# Revit family: Hager-VECTOR-Surface_mounted-IP65-With_Cover-With_DIN-NoHosted-ES-es
name_source: partatom
category: Electrical Equipment
units: mm (PartAtom-declared; Revit-internal decimal feet)

## family parameters
Always vertical = Yes
Cut with Voids When Loaded = No
Maintain Annotation Orientation = No
Panel Configuration = Two Columns, Circuits Across
Part Type = Panelboard
Room Calculation Point = No
Round Connector Dimension = Use Diameter
Shared = No
Work Plane-Based = Yes

## types (52) — shared parameters
Code hager = ADD-EC000214_EU
Default Elevation = 1200 mm
EF000003 - Método de montaje = Montado superficial (escayola)
EF000007 - Color = Gris
EF000024 - Resistente a UV = No
EF000116 - Número RAL = 7035
EF000118 - Con placa de montaje = No
EF001062 - Versión de CEM = No
EF001134 - Carril DIN = Yes
EF004462 - Tipo de cierre = Otros
EF005474 - Grado de protección (IP) = IP65
EF006306 - Con candado = No
ETIM class code = EC000214
ETIM class name = Small distribution board
HG000001 - Número de columnas = 1
HG000002-with door or cover-es = Yes
HG000003-Range-es = VECTOR
HG000005-Thickness-es = 2 mm  [stored 0.00656168 ft]
HG000006-Flush mounted-es = No
HG000009-Double swing door-es = No
HG000010-Asymmetric doors-es = No
HG000011-Empty rows from bottom-es = No
HG000012-Door swing angle-es = 90.00°
HG000013-Door on the left-es = No
HG000014-Door on the right-es = Yes
HG000015-Clearance visibility-es = Yes
HG000016-Door 3D visibility-es = Yes
HG000017-Distance between poles-es = 18 mm  [stored 0.0590551 ft]
HG000060-RAL-number = 7035
HG000099-Onfly Template ID-es-ES = 507532
Manufacturer = Hager
Name BIM&CO = Electricity
Name hager = ADD_Enclosures_EC000214
Reference = Template-Enclosure_EU-EC000214
Uniformat = Low Tension Service & Dist.
Uniformat code = D501001
zero-valued in all types: EF000218 - Profundidad de instalación, EF000332 - Altura de la instalación, EF000846 - Anchura de montaje, EF001131 - Profundidad interna, HG000007-Number of empty columns-es, HG000008-Number of empty rows-es

## per-type parameters (varying)
| type | BC_METADATA | EF000008 - Anchura | EF000040 - Altura | EF000049 - Profundidad | EF000266 - Número de filas | EF001088 - Posibilidad de extensión | EF002950 - Ancho en número de espacios modulares | EF006244 - Tapa/puerta transparente | EF009212 - Versión de la cubierta | EF015776 - Borne de tierra | EF015777 - Borne neutro | EF015941 - Puerta de transmisión de señal | HG000004-Manufacturer reference-es | HGEF000266-Número de filas | HGEF0002950-Ancho en número de espacios modulares |
| VECTOR-Surface_mounted_W310_H552_D151_12_Modular_Spacing-VE312F | {"ObjectGuid":"7676197e-38a1-4d90-8ddf-f4d718d94560","ModelGuid":"2ff45430-9ef3-4878-b9e2-60a5c988bfcc","VariantGuid":"09c07b7e-c6df-4300-81fb-90c715c4e884","Revision":"#6","VariantName":"VECTOR-Surface_mounted_W310_H552_D151_12_Modular_Spacing-VE312F"} | 310 mm  [stored 1.01706 ft] | 552 mm  [stored 1.81102 ft] | 151 mm  [stored 0.495407 ft] | 3 | Yes | 12 | No | Cerrado | Yes | No | Yes | VE312F | 3 | 12 |
| VECTOR-Surface_mounted_W310_H552_D151_12_Modular_Spacing-VE312PN | {"ObjectGuid":"7676197e-38a1-4d90-8ddf-f4d718d94560","ModelGuid":"2ff45430-9ef3-4878-b9e2-60a5c988bfcc","VariantGuid":"d662e2b3-0be1-45da-8c5f-6823ab68ee60","Revision":"#6","VariantName":"VECTOR-Surface_mounted_W310_H552_D151_12_Modular_Spacing-VE312PN"} | 310 mm  [stored 1.01706 ft] | 552 mm  [stored 1.81102 ft] | 151 mm  [stored 0.495407 ft] | 3 | Yes | 12 | Yes | Cerrado | No | No | Yes | VE312PN | 3 | 12 |
| VECTOR-Surface_mounted_W310_H552_D151_12_Modular_Spacing-VE312S | {"ObjectGuid":"7676197e-38a1-4d90-8ddf-f4d718d94560","ModelGuid":"2ff45430-9ef3-4878-b9e2-60a5c988bfcc","VariantGuid":"74c3a6b9-71b7-44c3-8c2b-f7d0cc669d50","Revision":"#6","VariantName":"VECTOR-Surface_mounted_W310_H552_D151_12_Modular_Spacing-VE312S"} | 310 mm  [stored 1.01706 ft] | 552 mm  [stored 1.81102 ft] | 151 mm  [stored 0.495407 ft] | 3 | Yes | 12 | No | Cerrado | Yes | Yes | Yes | VE312S | 3 | 12 |
| VECTOR-Surface_mounted_W310_H552_D151_12_Modular_Spacing-VE312SN | {"ObjectGuid":"7676197e-38a1-4d90-8ddf-f4d718d94560","ModelGuid":"2ff45430-9ef3-4878-b9e2-60a5c988bfcc","VariantGuid":"e56d686b-ab52-4e53-b856-6d5e133bc343","Revision":"#6","VariantName":"VECTOR-Surface_mounted_W310_H552_D151_12_Modular_Spacing-VE312SN"} | 310 mm  [stored 1.01706 ft] | 552 mm  [stored 1.81102 ft] | 151 mm  [stored 0.495407 ft] | 3 | Yes | 12 | Yes | Con muesca | No | No | Yes | VE312SN | 3 | 12 |
| VECTOR-Surface_mounted_W310_H552_D151_36_Modular_Spacing-VE312YN | {"ObjectGuid":"7676197e-38a1-4d90-8ddf-f4d718d94560","ModelGuid":"2ff45430-9ef3-4878-b9e2-60a5c988bfcc","VariantGuid":"98c29cbb-e30c-48a9-8ecf-4c3cb3c14188","Revision":"#6","VariantName":"VECTOR-Surface_mounted_W310_H552_D151_36_Modular_Spacing-VE312YN"} | 310 mm  [stored 1.01706 ft] | 552 mm  [stored 1.81102 ft] | 151 mm  [stored 0.495407 ft] | 3 | No | 36 | No | Con muesca | No | No | No | VE312YN | 3 | 36 |
| VECTOR-Surface_mounted_W418_H602_D151_12_Modular_Spacing-VE318E | {"ObjectGuid":"7676197e-38a1-4d90-8ddf-f4d718d94560","ModelGuid":"2ff45430-9ef3-4878-b9e2-60a5c988bfcc","VariantGuid":"475b0822-4809-4b8c-888b-22abb03a3c98","Revision":"#6","VariantName":"VECTOR-Surface_mounted_W418_H602_D151_12_Modular_Spacing-VE318E"} | 418 mm  [stored 1.37139 ft] | 602 mm  [stored 1.97507 ft] | 151 mm  [stored 0.495407 ft] | 3 | Yes | 12 | Yes | Con muesca | No | No | Yes | VE318E | 3 | 12 |
| VECTOR-Surface_mounted_W418_H602_D151_18_Modular_Spacing-VE318F | {"ObjectGuid":"7676197e-38a1-4d90-8ddf-f4d718d94560","ModelGuid":"2ff45430-9ef3-4878-b9e2-60a5c988bfcc","VariantGuid":"f558e8b9-6180-42f2-a197-0d709c570559","Revision":"#6","VariantName":"VECTOR-Surface_mounted_W418_H602_D151_18_Modular_Spacing-VE318F"} | 418 mm  [stored 1.37139 ft] | 602 mm  [stored 1.97507 ft] | 151 mm  [stored 0.495407 ft] | 3 | No | 18 | No | Con muesca | No | No | No | VE318F | 3 | 18 |
| VECTOR-Surface_mounted_W418_H602_D151_18_Modular_Spacing-VE318PN | {"ObjectGuid":"7676197e-38a1-4d90-8ddf-f4d718d94560","ModelGuid":"2ff45430-9ef3-4878-b9e2-60a5c988bfcc","VariantGuid":"032e2f7e-01fd-47bd-a41e-09040671e5f3","Revision":"#6","VariantName":"VECTOR-Surface_mounted_W418_H602_D151_18_Modular_Spacing-VE318PN"} | 418 mm  [stored 1.37139 ft] | 602 mm  [stored 1.97507 ft] | 151 mm  [stored 0.495407 ft] | 3 | Yes | 18 | Yes | Cerrado | No | No | Yes | VE318PN | 3 | 18 |
| VECTOR-Surface_mounted_W418_H602_D151_18_Modular_Spacing-VE318SN | {"ObjectGuid":"7676197e-38a1-4d90-8ddf-f4d718d94560","ModelGuid":"2ff45430-9ef3-4878-b9e2-60a5c988bfcc","VariantGuid":"efbdf9cf-3c92-46c7-b617-0941c19410cc","Revision":"#6","VariantName":"VECTOR-Surface_mounted_W418_H602_D151_18_Modular_Spacing-VE318SN"} | 418 mm  [stored 1.37139 ft] | 602 mm  [stored 1.97507 ft] | 151 mm  [stored 0.495407 ft] | 3 | Yes | 18 | Yes | Con muesca | No | No | Yes | VE318SN | 3 | 18 |
| VECTOR-Surface_mounted_W418_H602_D151_54_Modular_Spacing-VE318YN | {"ObjectGuid":"7676197e-38a1-4d90-8ddf-f4d718d94560","ModelGuid":"2ff45430-9ef3-4878-b9e2-60a5c988bfcc","VariantGuid":"d48118e3-bec0-49bb-86cb-bbeb98a66b20","Revision":"#6","VariantName":"VECTOR-Surface_mounted_W418_H602_D151_54_Modular_Spacing-VE318YN"} | 418 mm  [stored 1.37139 ft] | 602 mm  [stored 1.97507 ft] | 151 mm  [stored 0.495407 ft] | 3 | No | 54 | No | Con muesca | No | No | No | VE318YN | 3 | 54 |
| VECTOR-Surface_mounted_W310_H677_D151_12_Modular_Spacing-VE412E | {"ObjectGuid":"7676197e-38a1-4d90-8ddf-f4d718d94560","ModelGuid":"2ff45430-9ef3-4878-b9e2-60a5c988bfcc","VariantGuid":"5d06d5a9-9ca4-41c5-87c6-fb915dfe0d8b","Revision":"#6","VariantName":"VECTOR-Surface_mounted_W310_H677_D151_12_Modular_Spacing-VE412E"} | 310 mm  [stored 1.01706 ft] | 677 mm  [stored 2.22113 ft] | 151 mm  [stored 0.495407 ft] | 4 | No | 12 | No | Con muesca | No | No | No | VE412E | 4 | 12 |
| VECTOR-Surface_mounted_W310_H677_D151_12_Modular_Spacing-VE412F | {"ObjectGuid":"7676197e-38a1-4d90-8ddf-f4d718d94560","ModelGuid":"2ff45430-9ef3-4878-b9e2-60a5c988bfcc","VariantGuid":"3f0f81bd-a9ec-4c59-9d4b-21125c95fc9d","Revision":"#6","VariantName":"VECTOR-Surface_mounted_W310_H677_D151_12_Modular_Spacing-VE412F"} | 310 mm  [stored 1.01706 ft] | 677 mm  [stored 2.22113 ft] | 151 mm  [stored 0.495407 ft] | 4 | No | 12 | No | Con muesca | No | No | No | VE412F | 4 | 12 |
| VECTOR-Surface_mounted_W310_H677_D151_12_Modular_Spacing-VE412PN | {"ObjectGuid":"7676197e-38a1-4d90-8ddf-f4d718d94560","ModelGuid":"2ff45430-9ef3-4878-b9e2-60a5c988bfcc","VariantGuid":"f52910bb-d70f-4c31-a006-df6813b80de6","Revision":"#6","VariantName":"VECTOR-Surface_mounted_W310_H677_D151_12_Modular_Spacing-VE412PN"} | 310 mm  [stored 1.01706 ft] | 677 mm  [stored 2.22113 ft] | 151 mm  [stored 0.495407 ft] | 4 | Yes | 12 | Yes | Cerrado | No | No | Yes | VE412PN | 4 | 12 |
| VECTOR-Surface_mounted_W310_H677_D151_12_Modular_Spacing-VE412SN | {"ObjectGuid":"7676197e-38a1-4d90-8ddf-f4d718d94560","ModelGuid":"2ff45430-9ef3-4878-b9e2-60a5c988bfcc","VariantGuid":"240ba0fe-9974-479b-b4d4-dca84e01e18f","Revision":"#6","VariantName":"VECTOR-Surface_mounted_W310_H677_D151_12_Modular_Spacing-VE412SN"} | 310 mm  [stored 1.01706 ft] | 677 mm  [stored 2.22113 ft] | 151 mm  [stored 0.495407 ft] | 4 | Yes | 12 | Yes | Con muesca | No | No | Yes | VE412SN | 4 | 12 |
| VECTOR-Surface_mounted_W310_H677_D151_48_Modular_Spacing-VE412YN | {"ObjectGuid":"7676197e-38a1-4d90-8ddf-f4d718d94560","ModelGuid":"2ff45430-9ef3-4878-b9e2-60a5c988bfcc","VariantGuid":"da1bdaa6-d4ec-409c-a9a6-f41c97c9b8fe","Revision":"#6","VariantName":"VECTOR-Surface_mounted_W310_H677_D151_48_Modular_Spacing-VE412YN"} | 310 mm  [stored 1.01706 ft] | 677 mm  [stored 2.22113 ft] | 151 mm  [stored 0.495407 ft] | 4 | No | 48 | No | Con muesca | No | No | No | VE412YN | 4 | 48 |
| VECTOR-Surface_mounted_W111_H175_D93_3_Modular_Spacing-VE103E | {"ObjectGuid":"7676197e-38a1-4d90-8ddf-f4d718d94560","ModelGuid":"2ff45430-9ef3-4878-b9e2-60a5c988bfcc","VariantGuid":"a6bfe663-3398-4dc3-9527-c81ae7844b40","Revision":"#6","VariantName":"VECTOR-Surface_mounted_W111_H175_D93_3_Modular_Spacing-VE103E"} | 111 mm | 175 mm  [stored 0.574147 ft] | 93 mm  [stored 0.305118 ft] | 1 | Yes | 3 | Yes | Cerrado | No | No | Yes | VE103E | 1 | 3 |
| VECTOR-Surface_mounted_W111_H175_D93_3_Modular_Spacing-VE103F | {"ObjectGuid":"7676197e-38a1-4d90-8ddf-f4d718d94560","ModelGuid":"2ff45430-9ef3-4878-b9e2-60a5c988bfcc","VariantGuid":"4f2f4877-e92b-4e67-831e-3af6fcc14f5e","Revision":"#6","VariantName":"VECTOR-Surface_mounted_W111_H175_D93_3_Modular_Spacing-VE103F"} | 111 mm | 175 mm  [stored 0.574147 ft] | 93 mm  [stored 0.305118 ft] | 1 | No | 3 | No | Cerrado | No | No | No | VE103F | 1 | 3 |
| VECTOR-Surface_mounted_W111_H175_D93_3_Modular_Spacing-VE103PN | {"ObjectGuid":"7676197e-38a1-4d90-8ddf-f4d718d94560","ModelGuid":"2ff45430-9ef3-4878-b9e2-60a5c988bfcc","VariantGuid":"5a85d25c-552d-45d6-bf08-df9f925e4f1c","Revision":"#6","VariantName":"VECTOR-Surface_mounted_W111_H175_D93_3_Modular_Spacing-VE103PN"} | 111 mm | 175 mm  [stored 0.574147 ft] | 93 mm  [stored 0.305118 ft] | 1 | Yes | 3 | Yes | Con muesca | No | No | Yes | VE103PN | 1 | 3 |
| VECTOR-Surface_mounted_W165_H190_D113_3_Modular_Spacing-VE103PV | {"ObjectGuid":"7676197e-38a1-4d90-8ddf-f4d718d94560","ModelGuid":"2ff45430-9ef3-4878-b9e2-60a5c988bfcc","VariantGuid":"35ad04f8-5ec1-49cf-8fa8-633c2c9adcc9","Revision":"#6","VariantName":"VECTOR-Surface_mounted_W165_H190_D113_3_Modular_Spacing-VE103PV"} | 165 mm | 190 mm | 113 mm  [stored 0.370735 ft] | 1 | Yes | 3 | Yes | Con muesca | No | No | Yes | VE103PV | 1 | 3 |
| VECTOR-Surface_mounted_W111_H175_D93_3_Modular_Spacing-VE103SN | {"ObjectGuid":"7676197e-38a1-4d90-8ddf-f4d718d94560","ModelGuid":"2ff45430-9ef3-4878-b9e2-60a5c988bfcc","VariantGuid":"50be78f2-befc-4c6f-a964-1ca5ef27d623","Revision":"#6","VariantName":"VECTOR-Surface_mounted_W111_H175_D93_3_Modular_Spacing-VE103SN"} | 111 mm | 175 mm  [stored 0.574147 ft] | 93 mm  [stored 0.305118 ft] | 1 | Yes | 3 | Yes | Con muesca | No | No | Yes | VE103SN | 1 | 3 |
| VECTOR-Surface_mounted_W111_H175_D93_3_Modular_Spacing-VE103V | {"ObjectGuid":"7676197e-38a1-4d90-8ddf-f4d718d94560","ModelGuid":"2ff45430-9ef3-4878-b9e2-60a5c988bfcc","VariantGuid":"c3e4a6b7-9559-4506-86d4-1cabfba8d20a","Revision":"#6","VariantName":"VECTOR-Surface_mounted_W111_H175_D93_3_Modular_Spacing-VE103V"} | 111 mm | 175 mm  [stored 0.574147 ft] | 93 mm  [stored 0.305118 ft] | 1 | Yes | 3 | Yes | Con muesca | No | No | Yes | VE103V | 1 | 3 |
| VECTOR-Surface_mounted_W165_H190_D113_6_Modular_Spacing-VE106E | {"ObjectGuid":"7676197e-38a1-4d90-8ddf-f4d718d94560","ModelGuid":"2ff45430-9ef3-4878-b9e2-60a5c988bfcc","VariantGuid":"9db4d2a5-c4b1-464a-9f62-e375a0a22c3c","Revision":"#6","VariantName":"VECTOR-Surface_mounted_W165_H190_D113_6_Modular_Spacing-VE106E"} | 165 mm | 190 mm | 113 mm  [stored 0.370735 ft] | 1 | Yes | 6 | Yes | Con muesca | No | No | Yes | VE106E | 1 | 6 |
| VECTOR-Surface_mounted_W165_H190_D113_6_Modular_Spacing-VE106F | {"ObjectGuid":"7676197e-38a1-4d90-8ddf-f4d718d94560","ModelGuid":"2ff45430-9ef3-4878-b9e2-60a5c988bfcc","VariantGuid":"6dd902b2-9952-4533-911d-ae85f4253a8e","Revision":"#6","VariantName":"VECTOR-Surface_mounted_W165_H190_D113_6_Modular_Spacing-VE106F"} | 165 mm | 190 mm | 113 mm  [stored 0.370735 ft] | 1 | Yes | 6 | No | Cerrado | Yes | No | Yes | VE106F | 1 | 6 |
| VECTOR-Surface_mounted_W165_H190_D113_6_Modular_Spacing-VE106PN | {"ObjectGuid":"7676197e-38a1-4d90-8ddf-f4d718d94560","ModelGuid":"2ff45430-9ef3-4878-b9e2-60a5c988bfcc","VariantGuid":"a7c3d28d-d2b3-41f9-8a8b-f9d1aa6081a1","Revision":"#6","VariantName":"VECTOR-Surface_mounted_W165_H190_D113_6_Modular_Spacing-VE106PN"} | 165 mm | 190 mm | 113 mm  [stored 0.370735 ft] | 1 | Yes | 6 | Yes | Cerrado | No | No | Yes | VE106PN | 1 | 6 |
| VECTOR-Surface_mounted_W165_H190_D113_6_Modular_Spacing-VE106SN | {"ObjectGuid":"7676197e-38a1-4d90-8ddf-f4d718d94560","ModelGuid":"2ff45430-9ef3-4878-b9e2-60a5c988bfcc","VariantGuid":"a193b869-79e2-4774-a677-1030a370ae4b","Revision":"#6","VariantName":"VECTOR-Surface_mounted_W165_H190_D113_6_Modular_Spacing-VE106SN"} | 165 mm | 190 mm | 113 mm  [stored 0.370735 ft] | 1 | Yes | 6 | Yes | Con muesca | No | No | Yes | VE106SN | 1 | 6 |
| VECTOR-Surface_mounted_W165_H190_D113_6_Modular_Spacing-VE106YN | {"ObjectGuid":"7676197e-38a1-4d90-8ddf-f4d718d94560","ModelGuid":"2ff45430-9ef3-4878-b9e2-60a5c988bfcc","VariantGuid":"c08f610e-17d4-45dd-ac08-260515907206","Revision":"#6","VariantName":"VECTOR-Surface_mounted_W165_H190_D113_6_Modular_Spacing-VE106YN"} | 165 mm | 190 mm | 113 mm  [stored 0.370735 ft] | 1 | No | 6 | No | Con muesca | No | No | No | VE106YN | 1 | 6 |
| VECTOR-Surface_mounted_W237_H210_D114_10_Modular_Spacing-VE110E | {"ObjectGuid":"7676197e-38a1-4d90-8ddf-f4d718d94560","ModelGuid":"2ff45430-9ef3-4878-b9e2-60a5c988bfcc","VariantGuid":"4f2174b6-e1d4-48f9-89af-800d8d0edf4f","Revision":"#6","VariantName":"VECTOR-Surface_mounted_W237_H210_D114_10_Modular_Spacing-VE110E"} | 237 mm  [stored 0.777559 ft] | 210 mm  [stored 0.688976 ft] | 114 mm  [stored 0.374016 ft] | 1 | Yes | 10 | Yes | Cerrado | No | No | Yes | VE110E | 1 | 10 |
| VECTOR-Surface_mounted_W237_H210_D114_10_Modular_Spacing-VE110F | {"ObjectGuid":"7676197e-38a1-4d90-8ddf-f4d718d94560","ModelGuid":"2ff45430-9ef3-4878-b9e2-60a5c988bfcc","VariantGuid":"9b123fa9-478f-4f65-b593-7e5f77208d7a","Revision":"#6","VariantName":"VECTOR-Surface_mounted_W237_H210_D114_10_Modular_Spacing-VE110F"} | 237 mm  [stored 0.777559 ft] | 210 mm  [stored 0.688976 ft] | 114 mm  [stored 0.374016 ft] | 1 | Yes | 10 | No | Cerrado | Yes | No | Yes | VE110F | 1 | 10 |
| VECTOR-Surface_mounted_W237_H210_D114_10_Modular_Spacing-VE110PN | {"ObjectGuid":"7676197e-38a1-4d90-8ddf-f4d718d94560","ModelGuid":"2ff45430-9ef3-4878-b9e2-60a5c988bfcc","VariantGuid":"f17561fc-2e44-4a2d-b25e-59637b3b4c2c","Revision":"#6","VariantName":"VECTOR-Surface_mounted_W237_H210_D114_10_Modular_Spacing-VE110PN"} | 237 mm  [stored 0.777559 ft] | 210 mm  [stored 0.688976 ft] | 114 mm  [stored 0.374016 ft] | 1 | Yes | 10 | Yes | Cerrado | No | No | Yes | VE110PN | 1 | 10 |
| VECTOR-Surface_mounted_W237_H210_D114_10_Modular_Spacing-VE110SN | {"ObjectGuid":"7676197e-38a1-4d90-8ddf-f4d718d94560","ModelGuid":"2ff45430-9ef3-4878-b9e2-60a5c988bfcc","VariantGuid":"a77713d8-3899-48d3-9a9a-b8f702ad8935","Revision":"#6","VariantName":"VECTOR-Surface_mounted_W237_H210_D114_10_Modular_Spacing-VE110SN"} | 237 mm  [stored 0.777559 ft] | 210 mm  [stored 0.688976 ft] | 114 mm  [stored 0.374016 ft] | 1 | Yes | 10 | Yes | Cerrado | No | No | Yes | VE110SN | 1 | 10 |
| VECTOR-Surface_mounted_W237_H210_D114_10_Modular_Spacing-VE110YN | {"ObjectGuid":"7676197e-38a1-4d90-8ddf-f4d718d94560","ModelGuid":"2ff45430-9ef3-4878-b9e2-60a5c988bfcc","VariantGuid":"52e83467-be29-4a94-b422-609b071c3109","Revision":"#6","VariantName":"VECTOR-Surface_mounted_W237_H210_D114_10_Modular_Spacing-VE110YN"} | 237 mm  [stored 0.777559 ft] | 210 mm  [stored 0.688976 ft] | 114 mm  [stored 0.374016 ft] | 1 | No | 10 | No | Cerrado | No | No | No | VE110YN | 1 | 10 |
| VECTOR-Surface_mounted_W310_H302_D151_12_Modular_Spacing-VE112E | {"ObjectGuid":"7676197e-38a1-4d90-8ddf-f4d718d94560","ModelGuid":"2ff45430-9ef3-4878-b9e2-60a5c988bfcc","VariantGuid":"28786f7d-9f29-490c-9c5a-73e8101a8a4f","Revision":"#6","VariantName":"VECTOR-Surface_mounted_W310_H302_D151_12_Modular_Spacing-VE112E"} | 310 mm  [stored 1.01706 ft] | 302 mm  [stored 0.990814 ft] | 151 mm  [stored 0.495407 ft] | 1 | Yes | 12 | Yes | Cerrado | No | No | Yes | VE112E | 1 | 12 |
| VECTOR-Surface_mounted_W310_H302_D151_12_Modular_Spacing-VE112F | {"ObjectGuid":"7676197e-38a1-4d90-8ddf-f4d718d94560","ModelGuid":"2ff45430-9ef3-4878-b9e2-60a5c988bfcc","VariantGuid":"673a1995-d660-489b-919c-2f5e56b69380","Revision":"#6","VariantName":"VECTOR-Surface_mounted_W310_H302_D151_12_Modular_Spacing-VE112F"} | 310 mm  [stored 1.01706 ft] | 302 mm  [stored 0.990814 ft] | 151 mm  [stored 0.495407 ft] | 1 | Yes | 12 | No | Cerrado | Yes | No | Yes | VE112F | 1 | 12 |
| VECTOR-Surface_mounted_W310_H302_D151_12_Modular_Spacing-VE112PN | {"ObjectGuid":"7676197e-38a1-4d90-8ddf-f4d718d94560","ModelGuid":"2ff45430-9ef3-4878-b9e2-60a5c988bfcc","VariantGuid":"e139fb5b-79dc-4027-9886-ab01490814e3","Revision":"#6","VariantName":"VECTOR-Surface_mounted_W310_H302_D151_12_Modular_Spacing-VE112PN"} | 310 mm  [stored 1.01706 ft] | 302 mm  [stored 0.990814 ft] | 151 mm  [stored 0.495407 ft] | 1 | Yes | 12 | Yes | Cerrado | No | No | Yes | VE112PN | 1 | 12 |
| VECTOR-Surface_mounted_W310_H302_D151_12_Modular_Spacing-VE112SN | {"ObjectGuid":"7676197e-38a1-4d90-8ddf-f4d718d94560","ModelGuid":"2ff45430-9ef3-4878-b9e2-60a5c988bfcc","VariantGuid":"6b75f078-5268-40b1-a52e-ccbe10120955","Revision":"#6","VariantName":"VECTOR-Surface_mounted_W310_H302_D151_12_Modular_Spacing-VE112SN"} | 310 mm  [stored 1.01706 ft] | 302 mm  [stored 0.990814 ft] | 151 mm  [stored 0.495407 ft] | 1 | Yes | 12 | Yes | Cerrado | No | No | Yes | VE112SN | 1 | 12 |
| VECTOR-Surface_mounted_W310_H302_D151_12_Modular_Spacing-VE112YN | {"ObjectGuid":"7676197e-38a1-4d90-8ddf-f4d718d94560","ModelGuid":"2ff45430-9ef3-4878-b9e2-60a5c988bfcc","VariantGuid":"eac5e8e6-9914-4b44-b793-8d308d2b04b3","Revision":"#6","VariantName":"VECTOR-Surface_mounted_W310_H302_D151_12_Modular_Spacing-VE112YN"} | 310 mm  [stored 1.01706 ft] | 302 mm  [stored 0.990814 ft] | 151 mm  [stored 0.495407 ft] | 1 | No | 12 | No | Cerrado | No | No | No | VE112YN | 1 | 12 |
| VECTOR-Surface_mounted_W418_H302_D151_18_Modular_Spacing-VE118E | {"ObjectGuid":"7676197e-38a1-4d90-8ddf-f4d718d94560","ModelGuid":"2ff45430-9ef3-4878-b9e2-60a5c988bfcc","VariantGuid":"db5a86a7-e5c9-41f1-a654-7f59655b619c","Revision":"#6","VariantName":"VECTOR-Surface_mounted_W418_H302_D151_18_Modular_Spacing-VE118E"} | 418 mm  [stored 1.37139 ft] | 302 mm  [stored 0.990814 ft] | 151 mm  [stored 0.495407 ft] | 1 | Yes | 18 | Yes | Cerrado | No | No | Yes | VE118E | 1 | 18 |
| VECTOR-Surface_mounted_W418_H302_D151_18_Modular_Spacing-VE118F | {"ObjectGuid":"7676197e-38a1-4d90-8ddf-f4d718d94560","ModelGuid":"2ff45430-9ef3-4878-b9e2-60a5c988bfcc","VariantGuid":"b9a8843e-2b24-46b5-830f-a51bc6da0d01","Revision":"#6","VariantName":"VECTOR-Surface_mounted_W418_H302_D151_18_Modular_Spacing-VE118F"} | 418 mm  [stored 1.37139 ft] | 302 mm  [stored 0.990814 ft] | 151 mm  [stored 0.495407 ft] | 1 | No | 18 | No | Cerrado | No | No | No | VE118F | 1 | 18 |
| VECTOR-Surface_mounted_W418_H302_D151_18_Modular_Spacing-VE118PN | {"ObjectGuid":"7676197e-38a1-4d90-8ddf-f4d718d94560","ModelGuid":"2ff45430-9ef3-4878-b9e2-60a5c988bfcc","VariantGuid":"9d7fdd36-5b2f-4083-9019-a1076fd7aac4","Revision":"#6","VariantName":"VECTOR-Surface_mounted_W418_H302_D151_18_Modular_Spacing-VE118PN"} | 418 mm  [stored 1.37139 ft] | 302 mm  [stored 0.990814 ft] | 151 mm  [stored 0.495407 ft] | 1 | Yes | 18 | Yes | Cerrado | No | No | Yes | VE118PN | 1 | 18 |
| VECTOR-Surface_mounted_W418_H302_D151_18_Modular_Spacing-VE118SN | {"ObjectGuid":"7676197e-38a1-4d90-8ddf-f4d718d94560","ModelGuid":"2ff45430-9ef3-4878-b9e2-60a5c988bfcc","VariantGuid":"e8392f79-bdd9-4e8a-a1e2-1b2720487ab0","Revision":"#6","VariantName":"VECTOR-Surface_mounted_W418_H302_D151_18_Modular_Spacing-VE118SN"} | 418 mm  [stored 1.37139 ft] | 302 mm  [stored 0.990814 ft] | 151 mm  [stored 0.495407 ft] | 1 | Yes | 18 | Yes | Cerrado | No | No | Yes | VE118SN | 1 | 18 |
| VECTOR-Surface_mounted_W418_H302_D151_18_Modular_Spacing-VE118YN | {"ObjectGuid":"7676197e-38a1-4d90-8ddf-f4d718d94560","ModelGuid":"2ff45430-9ef3-4878-b9e2-60a5c988bfcc","VariantGuid":"0605acbc-cf4b-4ca2-aece-b2b961b36b81","Revision":"#6","VariantName":"VECTOR-Surface_mounted_W418_H302_D151_18_Modular_Spacing-VE118YN"} | 418 mm  [stored 1.37139 ft] | 302 mm  [stored 0.990814 ft] | 151 mm  [stored 0.495407 ft] | 1 | No | 18 | No | Cerrado | No | No | No | VE118YN | 1 | 18 |
| VECTOR-Surface_mounted_W310_H427_D151_12_Modular_Spacing-VE212E | {"ObjectGuid":"7676197e-38a1-4d90-8ddf-f4d718d94560","ModelGuid":"2ff45430-9ef3-4878-b9e2-60a5c988bfcc","VariantGuid":"27b202dd-bb43-4f53-8f65-fd7e56cdf63d","Revision":"#6","VariantName":"VECTOR-Surface_mounted_W310_H427_D151_12_Modular_Spacing-VE212E"} | 310 mm  [stored 1.01706 ft] | 427 mm  [stored 1.40092 ft] | 151 mm  [stored 0.495407 ft] | 2 | Yes | 12 | Yes | Cerrado | No | No | Yes | VE212E | 2 | 12 |
| VECTOR-Surface_mounted_W310_H427_D151_12_Modular_Spacing-VE212F | {"ObjectGuid":"7676197e-38a1-4d90-8ddf-f4d718d94560","ModelGuid":"2ff45430-9ef3-4878-b9e2-60a5c988bfcc","VariantGuid":"901427e8-d646-4434-9dcf-b815b657adde","Revision":"#6","VariantName":"VECTOR-Surface_mounted_W310_H427_D151_12_Modular_Spacing-VE212F"} | 310 mm  [stored 1.01706 ft] | 427 mm  [stored 1.40092 ft] | 151 mm  [stored 0.495407 ft] | 2 | Yes | 12 | No | Cerrado | Yes | No | Yes | VE212F | 2 | 12 |
| VECTOR-Surface_mounted_W310_H427_D151_12_Modular_Spacing-VE212PN | {"ObjectGuid":"7676197e-38a1-4d90-8ddf-f4d718d94560","ModelGuid":"2ff45430-9ef3-4878-b9e2-60a5c988bfcc","VariantGuid":"4a81d53c-3765-47b2-8302-51c8482f4505","Revision":"#6","VariantName":"VECTOR-Surface_mounted_W310_H427_D151_12_Modular_Spacing-VE212PN"} | 310 mm  [stored 1.01706 ft] | 427 mm  [stored 1.40092 ft] | 151 mm  [stored 0.495407 ft] | 2 | Yes | 12 | Yes | Cerrado | No | No | Yes | VE212PN | 2 | 12 |
| VECTOR-Surface_mounted_W310_H427_D151_12_Modular_Spacing-VE212SN | {"ObjectGuid":"7676197e-38a1-4d90-8ddf-f4d718d94560","ModelGuid":"2ff45430-9ef3-4878-b9e2-60a5c988bfcc","VariantGuid":"d7eaf0d1-5d5d-4045-ad67-f42f1e8be4dc","Revision":"#6","VariantName":"VECTOR-Surface_mounted_W310_H427_D151_12_Modular_Spacing-VE212SN"} | 310 mm  [stored 1.01706 ft] | 427 mm  [stored 1.40092 ft] | 151 mm  [stored 0.495407 ft] | 2 | Yes | 12 | Yes | Cerrado | No | No | Yes | VE212SN | 2 | 12 |
| VECTOR-Surface_mounted_W310_H427_D151_24_Modular_Spacing-VE212YN | {"ObjectGuid":"7676197e-38a1-4d90-8ddf-f4d718d94560","ModelGuid":"2ff45430-9ef3-4878-b9e2-60a5c988bfcc","VariantGuid":"0ab264c8-36d5-43bc-9e0d-ab1f36b2c06e","Revision":"#6","VariantName":"VECTOR-Surface_mounted_W310_H427_D151_24_Modular_Spacing-VE212YN"} | 310 mm  [stored 1.01706 ft] | 427 mm  [stored 1.40092 ft] | 151 mm  [stored 0.495407 ft] | 2 | No | 24 | No | Cerrado | Yes | No | No | VE212YN | 2 | 24 |
| VECTOR-Surface_mounted_W418_H452_D151_12_Modular_Spacing-VE218E | {"ObjectGuid":"7676197e-38a1-4d90-8ddf-f4d718d94560","ModelGuid":"2ff45430-9ef3-4878-b9e2-60a5c988bfcc","VariantGuid":"afcb6530-1ed2-4165-94cd-bf7deba50491","Revision":"#6","VariantName":"VECTOR-Surface_mounted_W418_H452_D151_12_Modular_Spacing-VE218E"} | 418 mm  [stored 1.37139 ft] | 452 mm  [stored 1.48294 ft] | 151 mm  [stored 0.495407 ft] | 2 | Yes | 12 | Yes | Con muesca | No | No | Yes | VE218E | 2 | 12 |
| VECTOR-Surface_mounted_W418_H452_D151_18_Modular_Spacing-VE218F | {"ObjectGuid":"7676197e-38a1-4d90-8ddf-f4d718d94560","ModelGuid":"2ff45430-9ef3-4878-b9e2-60a5c988bfcc","VariantGuid":"f82cedb5-9665-437f-8552-ea81ee233571","Revision":"#6","VariantName":"VECTOR-Surface_mounted_W418_H452_D151_18_Modular_Spacing-VE218F"} | 418 mm  [stored 1.37139 ft] | 452 mm  [stored 1.48294 ft] | 151 mm  [stored 0.495407 ft] | 2 | No | 18 | No | Con muesca | No | No | No | VE218F | 2 | 18 |
| VECTOR-Surface_mounted_W418_H452_D151_18_Modular_Spacing-VE218PN | {"ObjectGuid":"7676197e-38a1-4d90-8ddf-f4d718d94560","ModelGuid":"2ff45430-9ef3-4878-b9e2-60a5c988bfcc","VariantGuid":"e0896fdd-7220-4868-8b47-a63adcbb0759","Revision":"#6","VariantName":"VECTOR-Surface_mounted_W418_H452_D151_18_Modular_Spacing-VE218PN"} | 418 mm  [stored 1.37139 ft] | 452 mm  [stored 1.48294 ft] | 151 mm  [stored 0.495407 ft] | 2 | Yes | 18 | Yes | Cerrado | No | No | Yes | VE218PN | 2 | 18 |
| VECTOR-Surface_mounted_W418_H452_D151_18_Modular_Spacing-VE218SN | {"ObjectGuid":"7676197e-38a1-4d90-8ddf-f4d718d94560","ModelGuid":"2ff45430-9ef3-4878-b9e2-60a5c988bfcc","VariantGuid":"db0f2a25-5a26-4f2c-b7c7-05d1c3d771f1","Revision":"#6","VariantName":"VECTOR-Surface_mounted_W418_H452_D151_18_Modular_Spacing-VE218SN"} | 418 mm  [stored 1.37139 ft] | 452 mm  [stored 1.48294 ft] | 151 mm  [stored 0.495407 ft] | 2 | Yes | 18 | Yes | Con muesca | No | No | Yes | VE218SN | 2 | 18 |
| VECTOR-Surface_mounted_W418_H452_D151_36_Modular_Spacing-VE218YN | {"ObjectGuid":"7676197e-38a1-4d90-8ddf-f4d718d94560","ModelGuid":"2ff45430-9ef3-4878-b9e2-60a5c988bfcc","VariantGuid":"59a46448-b11e-4d48-9f92-9bdba3484a13","Revision":"#6","VariantName":"VECTOR-Surface_mounted_W418_H452_D151_36_Modular_Spacing-VE218YN"} | 418 mm  [stored 1.37139 ft] | 452 mm  [stored 1.48294 ft] | 151 mm  [stored 0.495407 ft] | 2 | No | 36 | Yes | Con muesca | No | No | Yes | VE218YN | 2 | 36 |
| VECTOR-Surface_mounted_W310_H552_D151_12_Modular_Spacing-VE312E | {"ObjectGuid":"7676197e-38a1-4d90-8ddf-f4d718d94560","ModelGuid":"2ff45430-9ef3-4878-b9e2-60a5c988bfcc","VariantGuid":"c1b76da2-46be-46dc-adc0-9c690d8c00af","Revision":"#6","VariantName":"VECTOR-Surface_mounted_W310_H552_D151_12_Modular_Spacing-VE312E"} | 310 mm  [stored 1.01706 ft] | 552 mm  [stored 1.81102 ft] | 151 mm  [stored 0.495407 ft] | 3 | Yes | 12 | Yes | Cerrado | No | No | Yes | VE312E | 3 | 12 |

note: [stored X ft] marks values corroborated as IEEE doubles in the binary element streams (Revit-internal decimal feet)

## geometry (parser evidence)
native form markers: Sweep x15
no freeform markers — native parametric forms only
